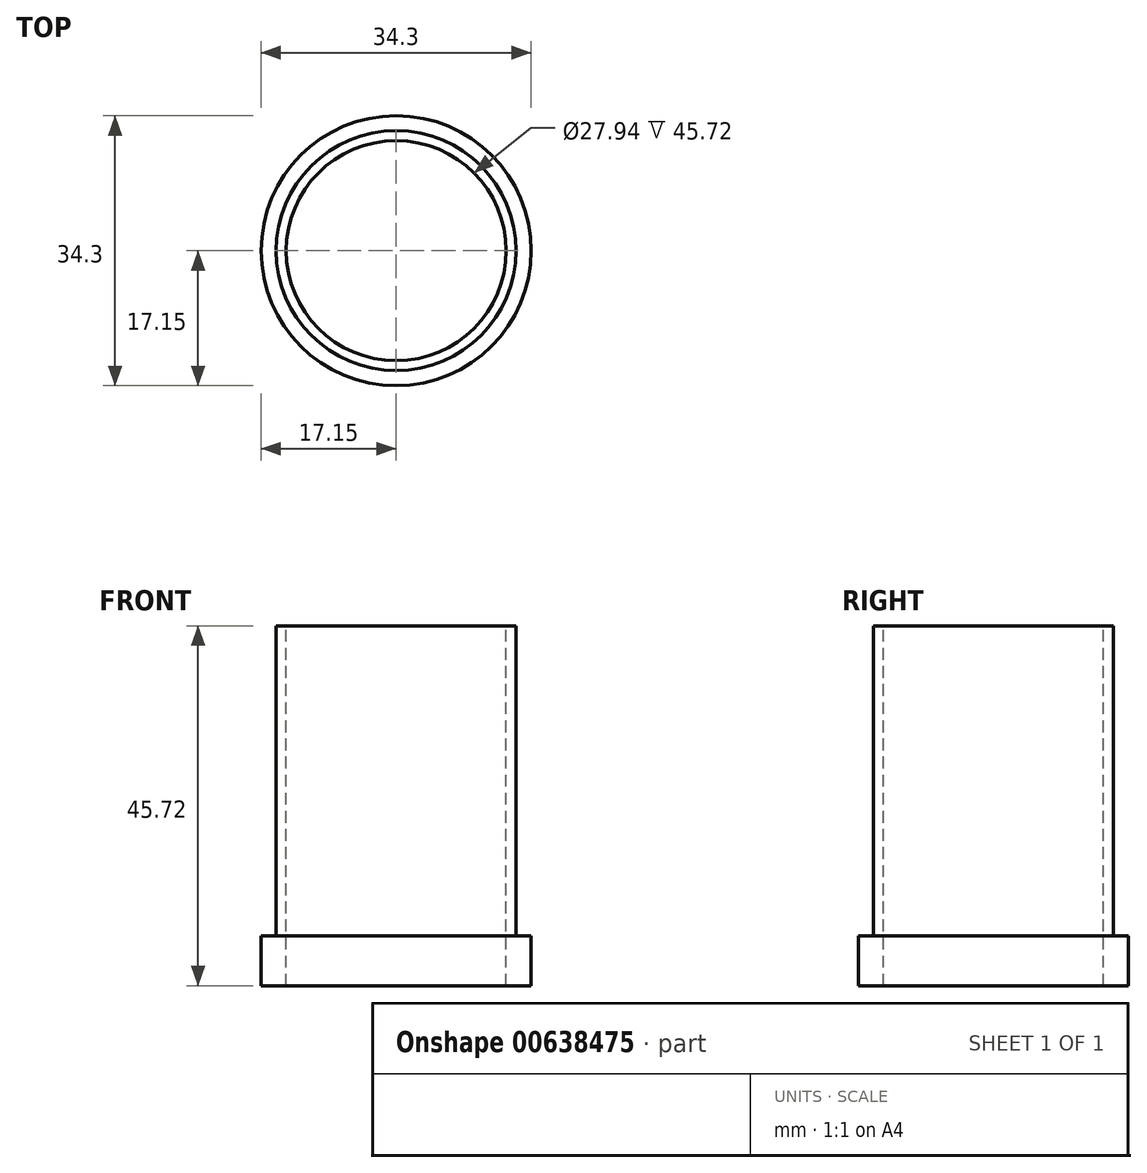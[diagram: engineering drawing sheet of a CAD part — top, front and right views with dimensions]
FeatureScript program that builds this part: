
annotation { "Feature Type Name" : "Feature", "Feature Type Description" : "" }
export const myFeature = defineFeature(function(context is Context, id is Id, definition is map)
    precondition{}
    {
        {
            var Q0;
            Q0=qCreatedBy(makeId("Top.planeOp"),FACE);
            var sketch = newSketch(context, id + "F0", { "sketchPlane" : qUnion([Q0])});
            skCircle(sketch, "E0", {"center": v(0, 0) * mm, "radius": 17.15 * mm});
            skCircle(sketch, "E1", {"center": v(0, 0) * mm, "radius": 13.97 * mm});
            skSolve(sketch);
        }
        {
            var Q0;
            Q0=makeQuery(id+"F0.imprint","IMPRINT",FACE,{"disambiguationData":[TD([[makeQuery(id+"F0.imprint","IMPRINT",EDGE,{"derivedFrom":sQuery(id+"F0.wireOp",EDGE,"E0")}),1.0]])]});
            extrude(context, id + "F1", {"entities" : qUnion([Q0]), "oppositeDirection" : true, "depth" : 6.35 * mm, "offsetDistance" : 25.4 * mm});
        }
        {
            var Q0;
            Q0=makeQuery(id+"F1.opExtrude","CAP_FACE",FACE,{"disambiguationData":[OSD([sQuery(id+"F0.wireOp",EDGE,"E0"),sQuery(id+"F0.wireOp",EDGE,"E1")])],"isStart":true});
            var sketch = newSketch(context, id + "F2", { "sketchPlane" : qUnion([Q0])});
            skCircle(sketch, "E2.0", {"center": v(0, 0) * mm, "radius": 13.97 * mm});
            skCircle(sketch, "E3", {"center": v(0, 0) * mm, "radius": 15.24 * mm});
            skSolve(sketch);
        }
        {
            var Q0;
            Q0=makeQuery(id+"F2.imprint","IMPRINT",FACE,{"disambiguationData":[TD([[makeQuery(id+"F2.imprint","IMPRINT",EDGE,{"derivedFrom":sQuery(id+"F2.wireOp",EDGE,"E2.0")}),-1.0]])]});
            extrude(context, id + "F3", {"entities" : qUnion([Q0]), "operationType" : NewBodyOperationType.ADD, "depth" : 39.37 * mm, "offsetDistance" : 25.4 * mm});
        }
    });
